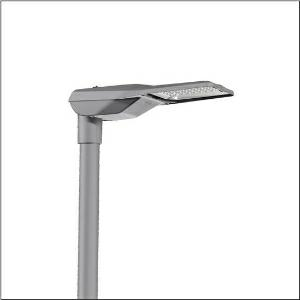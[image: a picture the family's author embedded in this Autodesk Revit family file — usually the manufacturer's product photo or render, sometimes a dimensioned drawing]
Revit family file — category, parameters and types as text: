
# Revit family: streetlight_sl_21_iq_mini___p0_5a_5xe2v31v08hb_1ab8
name_source: partatom
category: Lighting Fixtures
units: mm (PartAtom-declared; Revit-internal decimal feet)

## family parameters
Cut with Voids When Loaded = No
Host = Face
Light Source = No
Part Type = Normal
Room Calculation Point = No
Round Connector Dimension = Use Diameter
Shared = No

## types (1)
- --- (1 x LED, 9580 lm, 71 W, 3000K)
    Apparent Load = 71 VA
    CIE Flux Codes = 37 73 96 100 100
    Color Rendering = 70
    Color Temperature = 3000K
    Default Elevation = 1800 mm
    Description = Streetlight SL 21 iQ mini, mast luminaire, primary light control with lens, of PMMA, primary optical cover: cover, of toughened safety glass, transparent, light distribution: P0.5a, light emission: direct distribution, primary light characteristic: asymmetric, installation type: post-top, side-entry, LED, High Power LED, rated luminous flux: 9.580lm, luminous efficacy: 135lm/W, light colour: 730, colour temperature: 3000K, control gear: iQ-Street Remote, D4i with power reduction, control: pre-setting: logarithmic dimming characteristic, Street-Remote, Auto-Match, Temp-Guard, Lumen-Switch, Night-Set, Smart-Wire, Light-Fading, Desk-Remote (wireless, voltage-free reading and setting of iQ features in the workshop via application-optimized NFC function/RFID function), optimised constant luminous flux control (CLO 2.0), mains connection: 220..240V, AC, 50/60Hz, start of lifetime: 71W, end of service life: 75W, reduction: 30W, luminaire housing, of diecast aluminium, powder-coated, Siteco® metallic grey (DB 702S), corrosivity category C5 mid according to DIN EN ISO 12944, please order mast flange separately, inclination adjustable: 0°, 5°, 10°, 15°, sealing non-destructively replaceable, multi-level sealing system, length: 628mm, width: 235mm, height: 110mm, mast flange for spigot size: 42mm (side-entry): 5XC10008XM4, 60/48mm (side-entry/post-top): 5XC10108XM2, 76/60mm (side-entry/post-top): 5XC10108XM1, mounting height: 4..8m, Smart Interface above, protection rating (complete): IP66, insulation class (complete): insulation class II (safety insulation), certification: CE, ENEC, ENEC+, VDE, impact resistance: IK10, permissible operating ambient temperature for outdoor applications: -40..+50°C, standard-compliant lighting for roads and squares, packaging unit: 1 piece

Light Distribution: P0.5a
    Height = 110 mm
    Lamp = 1 x LED
    Lamp Light Flux = 9580 lm
    Lamp Power = 71 W
    Lamp count = 1
    Length = 625 mm
    Luminous efficacy = 135 lm/W
    Manufacturer = Siteco
    ModVariant = No
    Model = 5XE2V31V08HB
    Number of Poles = 1
    OnlyDefault = Yes
    Power Factor = 1
    Product Name = Streetlight SL 21 iQ mini | P0.5a
    Product group = mast luminaire | pylon top
    ProductGroupID = 6100
    Protection Class = Protection class II
    Protection Degree = IP 66
    RLX_Detail_Level = 1
    RLX_Emergency_Light_Flux = 0 lm
    RLX_Emergency_Type = 0
    RLX_Emergency_Type_DB = No
    RlxData = <blob elided: 25985 chars, md5=62908ae4>
    Socket = socket
    Standby Power = 0 W
    System Light Flux = 9580 lm
    System Power = 71 W
    Type Comments = factory setting: luminous flux: 100 % | dim-lin: 254 | 716 mA
    Type Image = l_1003515.jpg
    URL = http://relux.com
    VarID = @adj_070634
    Voltage = 0 V
    Weight = 0.00 kg
    Width = 234 mm

## geometry (parser evidence)
native form markers: Blend x4, Sweep x12
no freeform markers — native parametric forms only
